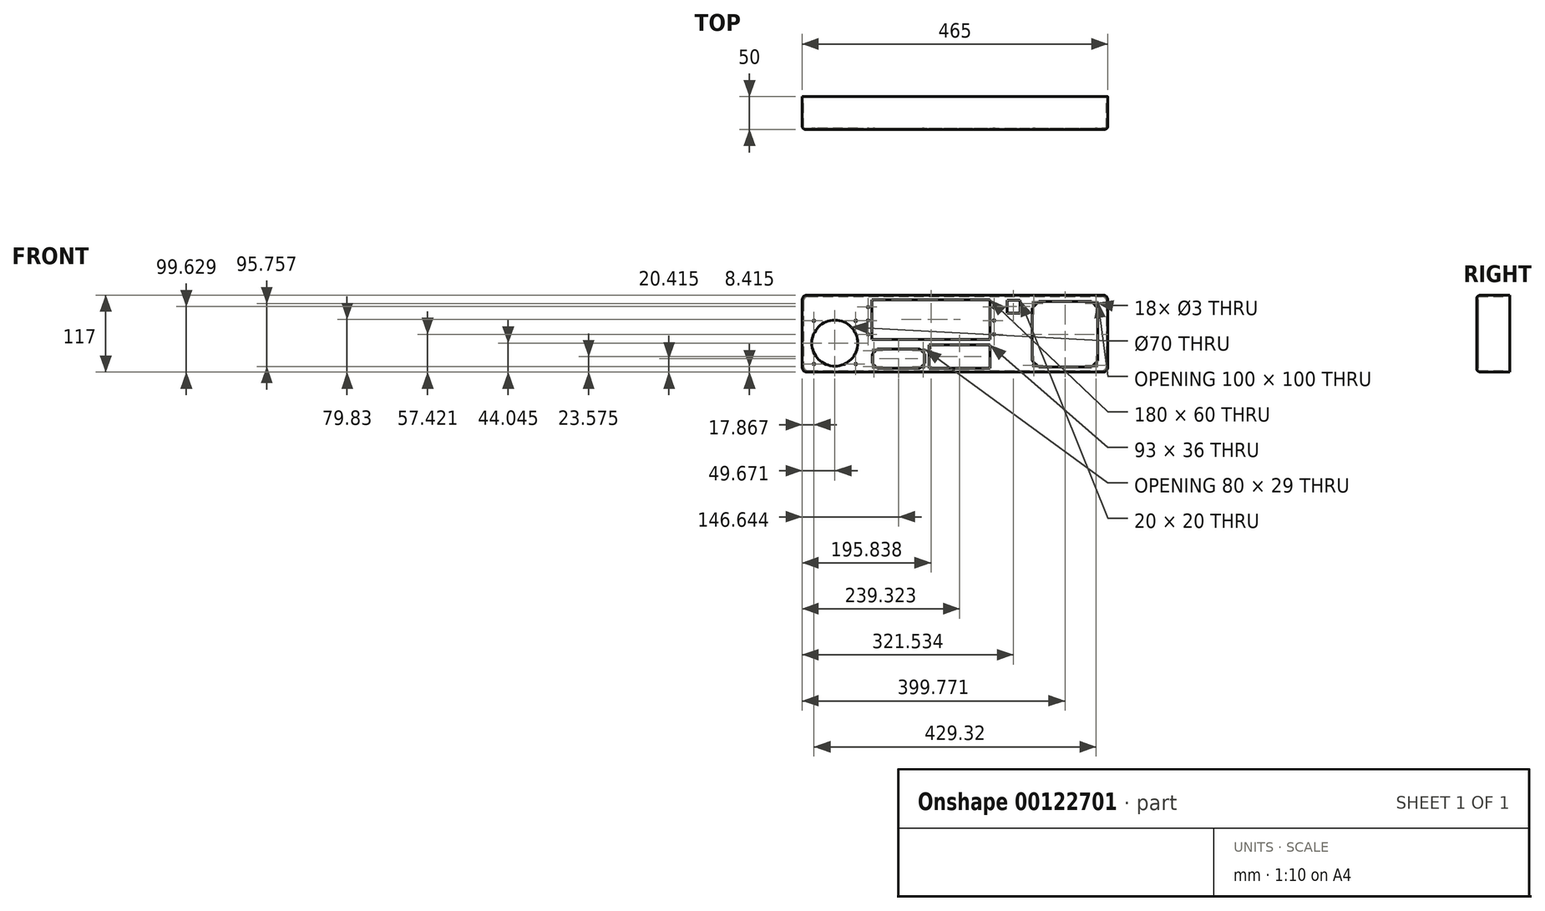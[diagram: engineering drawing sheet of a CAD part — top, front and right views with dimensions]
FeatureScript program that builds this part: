
annotation { "Feature Type Name" : "Feature", "Feature Type Description" : "" }
export const myFeature = defineFeature(function(context is Context, id is Id, definition is map)
    precondition{}
    {
        {
            var Q0;
            Q0=qCreatedBy(makeId("Front.planeOp"),FACE);
            var sketch = newSketch(context, id + "F0", { "sketchPlane" : qUnion([Q0])});
            skLineSegment(sketch, "E0.bottom", {"start": v(-245.15, 85.69) * mm, "end": v(219.85, 85.69) * mm});
            skLineSegment(sketch, "E0.top", {"start": v(-245.15, -31.31) * mm, "end": v(219.85, -31.31) * mm});
            skLineSegment(sketch, "E0.left", {"start": v(-245.15, 85.69) * mm, "end": v(-245.15, -31.31) * mm});
            skLineSegment(sketch, "E0.right", {"start": v(219.85, 85.69) * mm, "end": v(219.85, -31.31) * mm});
            skSolve(sketch);
        }
        {
            var Q0;
            Q0=qSketchRegion(id+"F0",true);
            var Q1;
            Q1=makeQuery(id+"F0.imprint","IMPRINT",FACE,{"disambiguationData":[TD([[makeQuery(id+"F0.imprint","IMPRINT",EDGE,{"derivedFrom":sQuery(id+"F0.wireOp",EDGE,"E0.bottom")}),-1.0]])]});
            extrude(context, id + "F1", {"entities" : qUnion([Q0, Q1]), "depth" : 50 * mm});
        }
        {
            var Q0;
            Q0=makeQuery(id+"F1.opExtrude","CAP_FACE",FACE,{"disambiguationData":[OSD([sQuery(id+"F0.wireOp",EDGE,"E0.bottom"),sQuery(id+"F0.wireOp",EDGE,"E0.top"),sQuery(id+"F0.wireOp",EDGE,"E0.left"),sQuery(id+"F0.wireOp",EDGE,"E0.right")])],"isStart":true});
            shell(context, id + "F2", {"entities" : qUnion([Q0]), "thickness" : 2 * mm});
        }
        {
            var Q0;
            Q0=makeQuery(id+"F1.opExtrude","CAP_FACE",FACE,{"disambiguationData":[OSD([sQuery(id+"F0.wireOp",EDGE,"E0.bottom"),sQuery(id+"F0.wireOp",EDGE,"E0.top"),sQuery(id+"F0.wireOp",EDGE,"E0.left"),sQuery(id+"F0.wireOp",EDGE,"E0.right")])],"isStart":false});
            var sketch = newSketch(context, id + "F3", { "sketchPlane" : qUnion([Q0])});
            skLineSegment(sketch, "E1.bottom", {"start": v(-139.31, 78.52) * mm, "end": v(40.69, 78.52) * mm});
            skLineSegment(sketch, "E1.top", {"start": v(-139.31, 18.52) * mm, "end": v(40.69, 18.52) * mm});
            skLineSegment(sketch, "E1.left", {"start": v(-139.31, 78.52) * mm, "end": v(-139.31, 18.52) * mm});
            skLineSegment(sketch, "E1.right", {"start": v(40.69, 78.52) * mm, "end": v(40.69, 18.52) * mm});
            skLineSegment(sketch, "E2.bottom", {"start": v(66.38, 78.32) * mm, "end": v(86.38, 78.32) * mm});
            skLineSegment(sketch, "E2.top", {"start": v(66.38, 58.32) * mm, "end": v(86.38, 58.32) * mm});
            skLineSegment(sketch, "E2.left", {"start": v(66.38, 78.32) * mm, "end": v(66.38, 58.32) * mm});
            skLineSegment(sketch, "E2.right", {"start": v(86.38, 78.32) * mm, "end": v(86.38, 58.32) * mm});
            skLineSegment(sketch, "E3.bottom", {"start": v(114.52, 76.11) * mm, "end": v(194.72, 76.11) * mm});
            skLineSegment(sketch, "E3.top", {"start": v(114.52, -23.89) * mm, "end": v(194.72, -23.89) * mm});
            skLineSegment(sketch, "E3.left", {"start": v(104.62, 66.21) * mm, "end": v(104.62, -13.99) * mm});
            skLineSegment(sketch, "E3.right", {"start": v(204.62, 66.21) * mm, "end": v(204.62, -13.99) * mm});
            skLineSegment(sketch, "E4.bottom", {"start": v(-128.05, -55.46) * mm, "end": v(-35.05, -55.46) * mm});
            skLineSegment(sketch, "E4.top", {"start": v(-128.05, -91.46) * mm, "end": v(-35.05, -91.46) * mm});
            skLineSegment(sketch, "E4.left", {"start": v(-128.05, -55.46) * mm, "end": v(-128.05, -91.46) * mm});
            skLineSegment(sketch, "E4.right", {"start": v(-35.05, -55.46) * mm, "end": v(-35.05, -91.46) * mm});
            skCircle(sketch, "E5", {"center": v(46.59, 67.55) * mm, "radius": 1.5 * mm});
            skCircle(sketch, "E6", {"center": v(46.59, 47.16) * mm, "radius": 1.5 * mm});
            skCircle(sketch, "E7", {"center": v(46.59, 26.05) * mm, "radius": 1.5 * mm});
            skLineSegment(sketch, "E8.bottom", {"start": v(-233.81, -59.67) * mm, "end": v(-156.81, -59.67) * mm});
            skLineSegment(sketch, "E8.top", {"start": v(-233.81, -136.67) * mm, "end": v(-156.81, -136.67) * mm});
            skLineSegment(sketch, "E8.left", {"start": v(-233.81, -59.67) * mm, "end": v(-233.81, -136.67) * mm});
            skLineSegment(sketch, "E8.right", {"start": v(-156.81, -59.67) * mm, "end": v(-156.81, -136.67) * mm});
            skCircle(sketch, "E9", {"center": v(107.52, 72.86) * mm, "radius": 1.5 * mm});
            skLineSegment(sketch, "E10", {"start": v(104.62, 66.21) * mm, "end": v(114.52, 76.11) * mm});
            skCircle(sketch, "E11", {"center": v(51.32, -84.07) * mm, "radius": 9.5 * mm});
            skLineSegment(sketch, "E12.bottom", {"start": v(34.38, -64.36) * mm, "end": v(127.38, -64.36) * mm});
            skLineSegment(sketch, "E12.top", {"start": v(34.38, -100.36) * mm, "end": v(127.38, -100.36) * mm});
            skLineSegment(sketch, "E12.left", {"start": v(34.38, -64.36) * mm, "end": v(34.38, -100.36) * mm});
            skLineSegment(sketch, "E12.right", {"start": v(127.38, -64.36) * mm, "end": v(127.38, -100.36) * mm});
            skCircle(sketch, "E13", {"center": v(81.35, -84.07) * mm, "radius": 9.5 * mm});
            skCircle(sketch, "E14", {"center": v(110.74, -84.07) * mm, "radius": 9.5 * mm});
            skCircle(sketch, "E15", {"center": v(38.38, -68.36) * mm, "radius": 1.5 * mm});
            skCircle(sketch, "E16", {"center": v(123.38, -96.36) * mm, "radius": 1.5 * mm});
            skLineSegment(sketch, "E17.bottom", {"start": v(-130.73, 3.6) * mm, "end": v(-66.28, 3.6) * mm});
            skLineSegment(sketch, "E17.top", {"start": v(-130.73, -25.4) * mm, "end": v(-66.28, -25.4) * mm});
            skLineSegment(sketch, "E17.left", {"start": v(-138.5, -4.17) * mm, "end": v(-138.5, -17.62) * mm});
            skLineSegment(sketch, "E17.right", {"start": v(-58.5, -4.17) * mm, "end": v(-58.5, -17.62) * mm});
            skCircle(sketch, "E18", {"center": v(-136, 1.1) * mm, "radius": 1.5 * mm});
            skCircle(sketch, "E19", {"center": v(-136, -22.9) * mm, "radius": 1.5 * mm});
            skCircle(sketch, "E20", {"center": v(-61, 1.1) * mm, "radius": 1.5 * mm});
            skCircle(sketch, "E21", {"center": v(-61, -22.9) * mm, "radius": 1.5 * mm});
            skLineSegment(sketch, "E22", {"start": v(104.62, -13.99) * mm, "end": v(114.52, -23.89) * mm});
            skLineSegment(sketch, "E23", {"start": v(194.72, -23.89) * mm, "end": v(204.62, -13.99) * mm});
            skLineSegment(sketch, "E24", {"start": v(194.72, 76.11) * mm, "end": v(204.62, 66.21) * mm});
            skCircle(sketch, "E25", {"center": v(107.52, -20.85) * mm, "radius": 1.5 * mm});
            skCircle(sketch, "E26", {"center": v(202.04, -20.85) * mm, "radius": 1.5 * mm});
            skCircle(sketch, "E27", {"center": v(202.04, 72.86) * mm, "radius": 1.5 * mm});
            skCircle(sketch, "E28", {"center": v(-195.48, 12.73) * mm, "radius": 35 * mm});
            skLineSegment(sketch, "E29", {"start": v(-138.5, -4.17) * mm, "end": v(-130.73, 3.6) * mm});
            skLineSegment(sketch, "E30", {"start": v(-66.28, 3.6) * mm, "end": v(-58.5, -4.17) * mm});
            skLineSegment(sketch, "E31", {"start": v(-58.5, -17.62) * mm, "end": v(-66.28, -25.4) * mm});
            skLineSegment(sketch, "E32", {"start": v(-138.5, -17.62) * mm, "end": v(-130.73, -25.4) * mm});
            skCircle(sketch, "E33", {"center": v(-144.85, 67.55) * mm, "radius": 1.5 * mm});
            skCircle(sketch, "E34", {"center": v(-144.85, 47.16) * mm, "radius": 1.5 * mm});
            skCircle(sketch, "E35", {"center": v(-144.85, 26.05) * mm, "radius": 1.5 * mm});
            skCircle(sketch, "E36", {"center": v(-227.28, 46.66) * mm, "radius": 1.5 * mm});
            skCircle(sketch, "E37", {"center": v(-227.28, -19.1) * mm, "radius": 1.5 * mm});
            skCircle(sketch, "E38", {"center": v(-163.64, -19.1) * mm, "radius": 1.5 * mm});
            skLineSegment(sketch, "E39.bottom", {"start": v(-52.33, 10.27) * mm, "end": v(40.67, 10.27) * mm});
            skLineSegment(sketch, "E39.top", {"start": v(-52.33, -25.73) * mm, "end": v(40.67, -25.73) * mm});
            skLineSegment(sketch, "E39.left", {"start": v(-52.33, 10.27) * mm, "end": v(-52.33, -25.73) * mm});
            skLineSegment(sketch, "E39.right", {"start": v(40.67, 10.27) * mm, "end": v(40.67, -25.73) * mm});
            skCircle(sketch, "E40", {"center": v(-163.68, 46.66) * mm, "radius": 1.5 * mm});
            skSolve(sketch);
        }
        {
            var Q0;
            Q0=makeQuery(id+"F1.opExtrude","SWEPT_EDGE",EDGE,{"disambiguationData":[OSD([sQuery(id+"F0.wireOp",EDGE,"E0.bottom"),sQuery(id+"F0.wireOp",EDGE,"E0.left")])]});
            var Q1;
            Q1=makeQuery(id+"F1.opExtrude","SWEPT_EDGE",EDGE,{"disambiguationData":[OSD([sQuery(id+"F0.wireOp",EDGE,"E0.bottom"),sQuery(id+"F0.wireOp",EDGE,"E0.right")])]});
            var Q2;
            Q2=makeQuery(id+"F1.opExtrude","SWEPT_EDGE",EDGE,{"disambiguationData":[OSD([sQuery(id+"F0.wireOp",EDGE,"E0.top"),sQuery(id+"F0.wireOp",EDGE,"E0.right")])]});
            var Q3;
            Q3=makeQuery(id+"F1.opExtrude","SWEPT_EDGE",EDGE,{"disambiguationData":[OSD([sQuery(id+"F0.wireOp",EDGE,"E0.top"),sQuery(id+"F0.wireOp",EDGE,"E0.left")])]});
            var Q4;
            Q4=makeQuery(id+"F2.opShell","OFFSET_EDGE",EDGE,{"disambiguationData":[OSD([sQuery(id+"F0.wireOp",EDGE,"E0.bottom"),sQuery(id+"F0.wireOp",EDGE,"E0.left")])]});
            var Q5;
            Q5=makeQuery(id+"F2.opShell","OFFSET_EDGE",EDGE,{"disambiguationData":[OSD([sQuery(id+"F0.wireOp",EDGE,"E0.top"),sQuery(id+"F0.wireOp",EDGE,"E0.left")])]});
            var Q6;
            Q6=makeQuery(id+"F2.opShell","OFFSET_EDGE",EDGE,{"disambiguationData":[OSD([sQuery(id+"F0.wireOp",EDGE,"E0.top"),sQuery(id+"F0.wireOp",EDGE,"E0.right")])]});
            var Q7;
            Q7=makeQuery(id+"F2.opShell","OFFSET_EDGE",EDGE,{"disambiguationData":[OSD([sQuery(id+"F0.wireOp",EDGE,"E0.bottom"),sQuery(id+"F0.wireOp",EDGE,"E0.right")])]});
            fillet(context, id + "F4", {"entities" : qUnion([Q0, Q1, Q2, Q3, Q4, Q5, Q6, Q7]), "radius" : 7 * mm, "tangentPropagation" : true, "allowEdgeOverflow" : false});
        }
        {
            var Q0;
            Q0=qSketchRegion(id+"F3",true);
            extrude(context, id + "F5", {"entities" : qUnion([Q0]), "operationType" : NewBodyOperationType.REMOVE, "oppositeDirection" : true, "depth" : 25 * mm});
        }
        {
            var Q0;
            {var subQ0=sQuery(id+"F0.wireOp",EDGE,"E0.right");var subQ1=sQuery(id+"F0.wireOp",EDGE,"E0.bottom");Q0=makeQuery(id+"F4.opFillet","BLEND_EDGE",EDGE,{"blendedFrom":[makeQuery(id+"F1.opExtrude","SWEPT_EDGE",EDGE,{"disambiguationData":[OSD([subQ1,subQ0])]}),makeQuery(id+"F1.opExtrude","CAP_FACE",FACE,{"disambiguationData":[OSD([subQ1,sQuery(id+"F0.wireOp",EDGE,"E0.top"),sQuery(id+"F0.wireOp",EDGE,"E0.left"),subQ0])],"isStart":false})],"blendedInto":[makeQuery(id+"F1.opExtrude","CAP_FACE",FACE,{"disambiguationData":[OSD([subQ1,sQuery(id+"F0.wireOp",EDGE,"E0.top"),sQuery(id+"F0.wireOp",EDGE,"E0.left"),subQ0])],"isStart":false})]});}
            fillet(context, id + "F6", {"entities" : qUnion([Q0]), "radius" : 5 * mm, "tangentPropagation" : true, "allowEdgeOverflow" : false});
        }
    });
